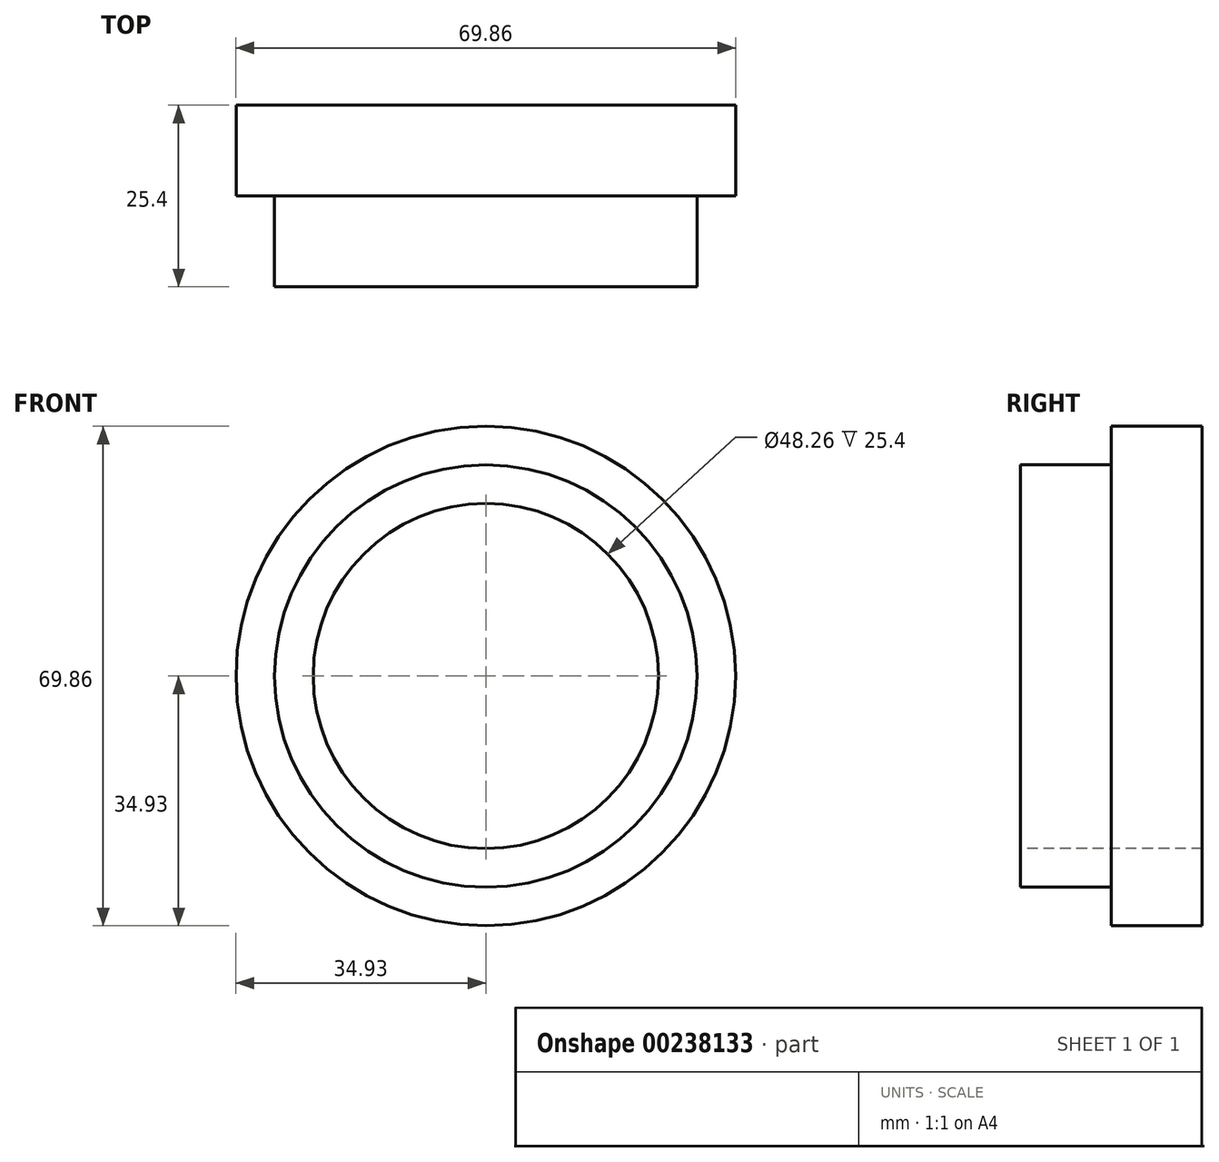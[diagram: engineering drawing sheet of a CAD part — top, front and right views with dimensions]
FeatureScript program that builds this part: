
annotation { "Feature Type Name" : "Feature", "Feature Type Description" : "" }
export const myFeature = defineFeature(function(context is Context, id is Id, definition is map)
    precondition{}
    {
        {
            var Q0;
            Q0=qCreatedBy(makeId("Right.planeOp"),FACE);
            var sketch = newSketch(context, id + "F0", { "sketchPlane" : qUnion([Q0])});
            skLineSegment(sketch, "E0.bottom", {"start": v(0, 0) * mm, "end": v(12.7, 0) * mm});
            skLineSegment(sketch, "E0.top", {"start": v(0, -34.93) * mm, "end": v(12.7, -34.93) * mm});
            skLineSegment(sketch, "E0.left", {"start": v(0, 0) * mm, "end": v(0, -34.93) * mm});
            skLineSegment(sketch, "E0.right", {"start": v(12.7, 0) * mm, "end": v(12.7, -34.93) * mm});
            skPoint(sketch, "E1.oppositeSnap0", {"position": v(12.7, -17.46) * mm});
            skLineSegment(sketch, "E2.bottom", {"start": v(0, 0) * mm, "end": v(-12.7, 0) * mm});
            skLineSegment(sketch, "E2.top", {"start": v(0, 29.53) * mm, "end": v(-12.7, 29.53) * mm});
            skLineSegment(sketch, "E2.left", {"start": v(0, 0) * mm, "end": v(0, 29.53) * mm});
            skLineSegment(sketch, "E2.right", {"start": v(-12.7, 0) * mm, "end": v(-12.7, 29.53) * mm});
            skSolve(sketch);
        }
        {
            var Q0;
            Q0=makeQuery(id+"F0.imprint","IMPRINT",FACE,{"disambiguationData":[TD([[makeQuery(id+"F0.imprint","IMPRINT",EDGE,{"derivedFrom":sQuery(id+"F0.wireOp",EDGE,"E0.bottom")}),-1.0]])]});
            var Q1;
            Q1=sQuery(id+"F0.wireOp",EDGE,"E0.bottom");
            revolve(context, id + "F1", {"entities" : qUnion([Q0]), "axis" : qUnion([Q1]), "revolveType" : RevolveType.FULL});
        }
        {
            var Q0;
            Q0 = qSketchRegion(id + "F0", true);
            var Q1;
            Q1=makeQuery(id+"F1.opRevolve","SWEPT_FACE",FACE,{"disambiguationData":[OSD([sQuery(id+"F0.wireOp",EDGE,"E0.top")])]});
            revolve(context, id + "F2", {"operationType" : NewBodyOperationType.ADD, "entities" : qUnion([Q0]), "axis" : qUnion([Q1]), "revolveType" : RevolveType.FULL});
        }
        {
            var Q0;
            Q0=makeQuery(id+"F2.opRevolve","SWEPT_FACE",FACE,{"disambiguationData":[OSD([sQuery(id+"F0.wireOp",EDGE,"E2.right")])]});
            var sketch = newSketch(context, id + "F3", { "sketchPlane" : qUnion([Q0])});
            skCircle(sketch, "E3", {"center": v(0, 0) * mm, "radius": 24.13 * mm});
            skSolve(sketch);
        }
        {
            var Q0;
            Q0=makeQuery(id+"F3.imprint","IMPRINT",FACE,{"disambiguationData":[TD([[makeQuery(id+"F3.imprint","IMPRINT",EDGE,{"derivedFrom":sQuery(id+"F3.wireOp",EDGE,"E3")}),1.0]])]});
            extrude(context, id + "F4", {"entities" : qUnion([Q0]), "operationType" : NewBodyOperationType.REMOVE, "oppositeDirection" : true, "depth" : 25.4 * mm});
        }
    });
